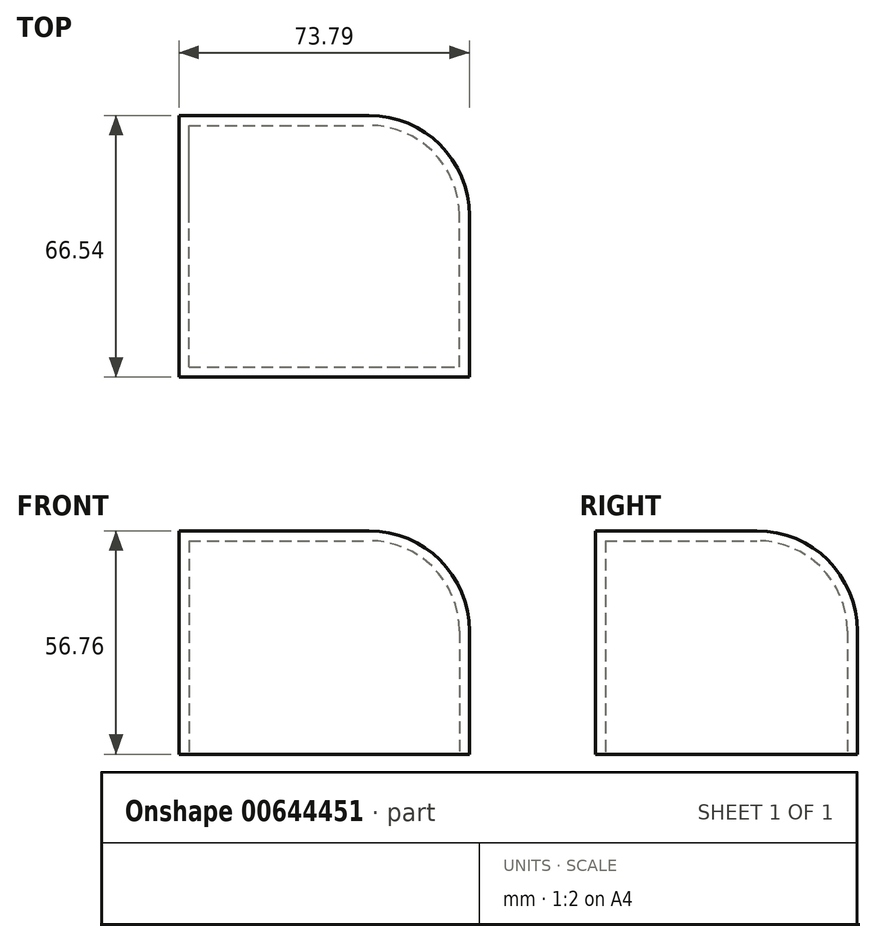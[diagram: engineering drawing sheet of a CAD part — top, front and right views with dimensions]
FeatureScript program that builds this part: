
annotation { "Feature Type Name" : "Feature", "Feature Type Description" : "" }
export const myFeature = defineFeature(function(context is Context, id is Id, definition is map)
    precondition{}
    {
        {
            var Q0;
            Q0=qCreatedBy(makeId("Top.planeOp"),FACE);
            var sketch = newSketch(context, id + "F0", { "sketchPlane" : qUnion([Q0])});
            skLineSegment(sketch, "E0.bottom", {"start": v(-39.05, 0) * mm, "end": v(34.74, 0) * mm});
            skLineSegment(sketch, "E0.top", {"start": v(-39.05, 66.54) * mm, "end": v(34.74, 66.54) * mm});
            skLineSegment(sketch, "E0.left", {"start": v(-39.05, 0) * mm, "end": v(-39.05, 66.54) * mm});
            skLineSegment(sketch, "E0.right", {"start": v(34.74, 0) * mm, "end": v(34.74, 66.54) * mm});
            skSolve(sketch);
        }
        {
            var Q0;
            Q0=makeQuery(id+"F0.imprint","IMPRINT",FACE,{"disambiguationData":[TD([[makeQuery(id+"F0.imprint","IMPRINT",EDGE,{"derivedFrom":sQuery(id+"F0.wireOp",EDGE,"E0.bottom")}),1.0]])]});
            extrude(context, id + "F1", {"entities" : qUnion([Q0]), "depth" : 56.76 * mm, "offsetDistance" : 25.4 * mm});
        }
        {
            var Q0;
            Q0=makeQuery(id+"F1.opExtrude","CAP_EDGE",EDGE,{"disambiguationData":[OSD([sQuery(id+"F0.wireOp",EDGE,"E0.top")])],"isStart":false});
            var Q1;
            Q1=makeQuery(id+"F1.opExtrude","SWEPT_EDGE",EDGE,{"disambiguationData":[OSD([sQuery(id+"F0.wireOp",EDGE,"E0.top"),sQuery(id+"F0.wireOp",EDGE,"E0.right")])]});
            var Q2;
            Q2=makeQuery(id+"F1.opExtrude","CAP_EDGE",EDGE,{"disambiguationData":[OSD([sQuery(id+"F0.wireOp",EDGE,"E0.right")])],"isStart":false});
            fillet(context, id + "F2", {"entities" : qUnion([Q0, Q1, Q2]), "radius" : 25.5 * mm, "tangentPropagation" : true, "allowEdgeOverflow" : false});
        }
        {
            var Q0;
            Q0=makeQuery(id+"F1.opExtrude","CAP_FACE",FACE,{"disambiguationData":[OSD([sQuery(id+"F0.wireOp",EDGE,"E0.bottom"),sQuery(id+"F0.wireOp",EDGE,"E0.top"),sQuery(id+"F0.wireOp",EDGE,"E0.left"),sQuery(id+"F0.wireOp",EDGE,"E0.right")])],"isStart":true});
            shell(context, id + "F3", {"entities" : qUnion([Q0]), "thickness" : 2.54 * mm});
        }
    });
